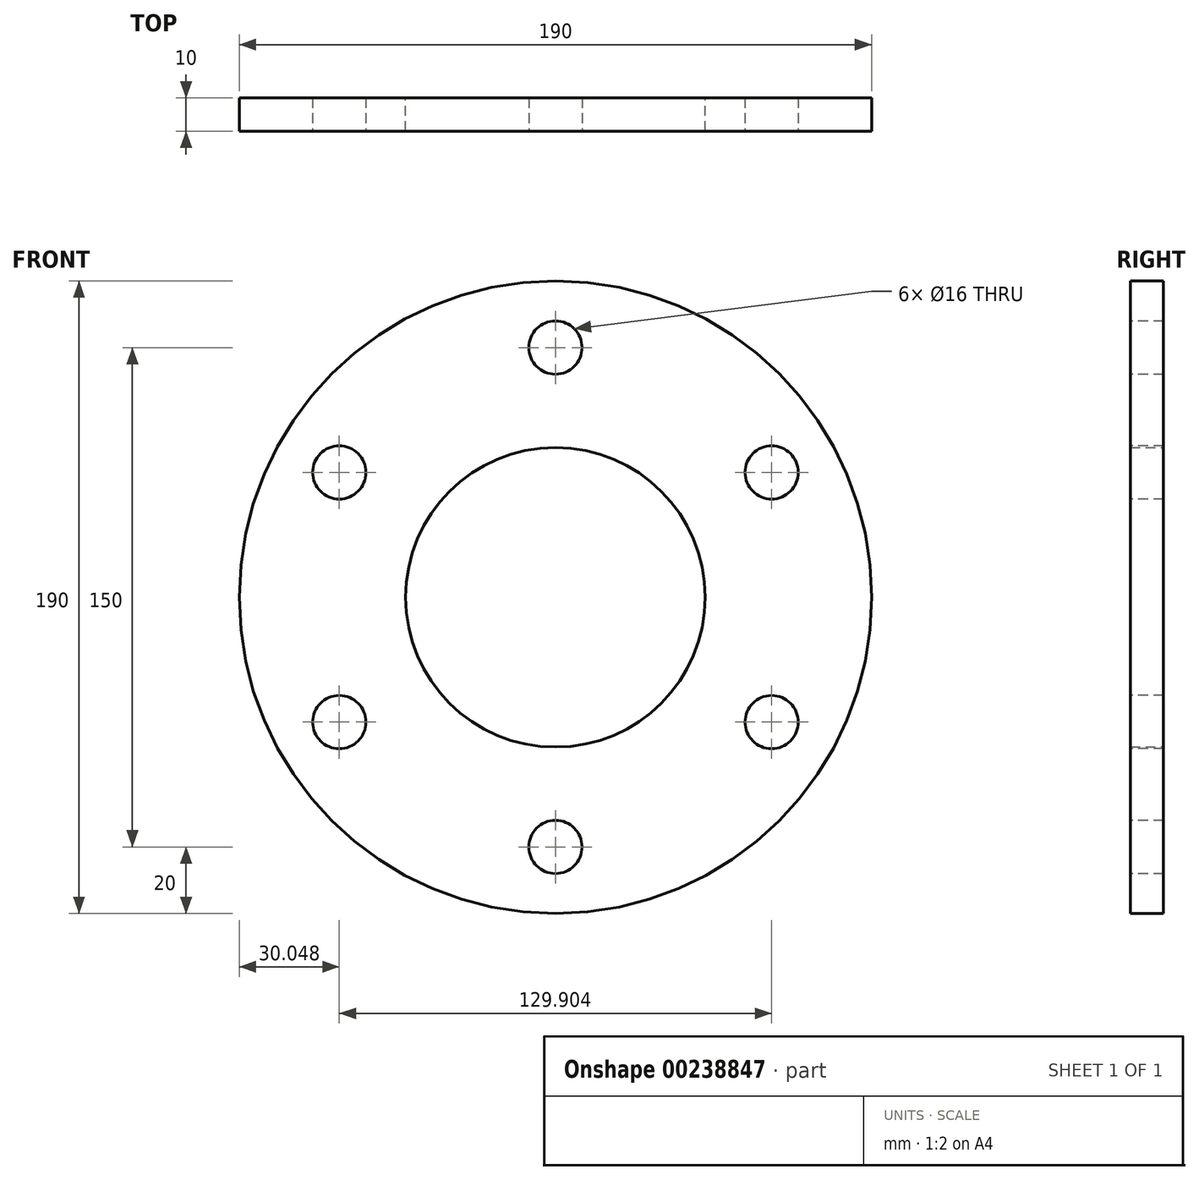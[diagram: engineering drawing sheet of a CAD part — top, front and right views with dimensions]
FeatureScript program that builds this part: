
annotation { "Feature Type Name" : "Feature", "Feature Type Description" : "" }
export const myFeature = defineFeature(function(context is Context, id is Id, definition is map)
    precondition{}
    {
        {
            var Q0;
            Q0=qCreatedBy(makeId("Front.planeOp"),FACE);
            var sketch = newSketch(context, id + "F0", { "sketchPlane" : qUnion([Q0])});
            skCircle(sketch, "E0", {"center": v(0, 0) * mm, "radius": 95 * mm});
            skCircle(sketch, "E1", {"center": v(0, 0) * mm, "radius": 45 * mm});
            skSolve(sketch);
        }
        {
            var Q0;
            Q0=makeQuery(id+"F0.imprint","IMPRINT",FACE,{"disambiguationData":[TD([[makeQuery(id+"F0.imprint","IMPRINT",EDGE,{"derivedFrom":sQuery(id+"F0.wireOp",EDGE,"E0")}),1.0]])]});
            extrude(context, id + "F1", {"entities" : qUnion([Q0]), "depth" : 10 * mm});
        }
        {
            var Q0;
            Q0=makeQuery(id+"F1.opExtrude","CAP_FACE",FACE,{"disambiguationData":[OSD([sQuery(id+"F0.wireOp",EDGE,"E0"),sQuery(id+"F0.wireOp",EDGE,"E1")])],"isStart":false});
            var sketch = newSketch(context, id + "F2", { "sketchPlane" : qUnion([Q0])});
            skCircle(sketch, "E2", {"center": v(0, 75) * mm, "radius": 8 * mm});
            skCircle(sketch, "E3.1.0", {"center": v(-64.95, 37.5) * mm, "radius": 8 * mm});
            skCircle(sketch, "E3.2.0", {"center": v(-64.95, -37.5) * mm, "radius": 8 * mm});
            skPoint(sketch, "E3.center", {"position": v(0, 0) * mm});
            skCircle(sketch, "E4.1.3.0", {"center": v(0, -75) * mm, "radius": 8 * mm});
            skCircle(sketch, "E4.1.4.0", {"center": v(64.95, -37.5) * mm, "radius": 8 * mm});
            skCircle(sketch, "E4.1.5.0", {"center": v(64.95, 37.5) * mm, "radius": 8 * mm});
            skSolve(sketch);
        }
        {
            var Q0;
            Q0=makeQuery(id+"F2.imprint","IMPRINT",FACE,{"disambiguationData":[TD([[makeQuery(id+"F2.imprint","IMPRINT",EDGE,{"derivedFrom":sQuery(id+"F2.wireOp",EDGE,"E2")}),1.0]])]});
            var Q1;
            Q1=makeQuery(id+"F2.imprint","IMPRINT",FACE,{"disambiguationData":[TD([[makeQuery(id+"F2.imprint","IMPRINT",EDGE,{"derivedFrom":sQuery(id+"F2.wireOp",EDGE,"E4.1.5.0")}),1.0]])]});
            var Q2;
            Q2=makeQuery(id+"F2.imprint","IMPRINT",FACE,{"disambiguationData":[TD([[makeQuery(id+"F2.imprint","IMPRINT",EDGE,{"derivedFrom":sQuery(id+"F2.wireOp",EDGE,"E4.1.4.0")}),1.0]])]});
            var Q3;
            Q3=makeQuery(id+"F2.imprint","IMPRINT",FACE,{"disambiguationData":[TD([[makeQuery(id+"F2.imprint","IMPRINT",EDGE,{"derivedFrom":sQuery(id+"F2.wireOp",EDGE,"E4.1.3.0")}),1.0]])]});
            var Q4;
            Q4=makeQuery(id+"F2.imprint","IMPRINT",FACE,{"disambiguationData":[TD([[makeQuery(id+"F2.imprint","IMPRINT",EDGE,{"derivedFrom":sQuery(id+"F2.wireOp",EDGE,"E3.2.0")}),1.0]])]});
            var Q5;
            Q5=makeQuery(id+"F2.imprint","IMPRINT",FACE,{"disambiguationData":[TD([[makeQuery(id+"F2.imprint","IMPRINT",EDGE,{"derivedFrom":sQuery(id+"F2.wireOp",EDGE,"E3.1.0")}),1.0]])]});
            extrude(context, id + "F3", {"entities" : qUnion([Q0, Q1, Q2, Q3, Q4, Q5]), "operationType" : NewBodyOperationType.REMOVE, "oppositeDirection" : true, "depth" : 25 * mm});
        }
    });
